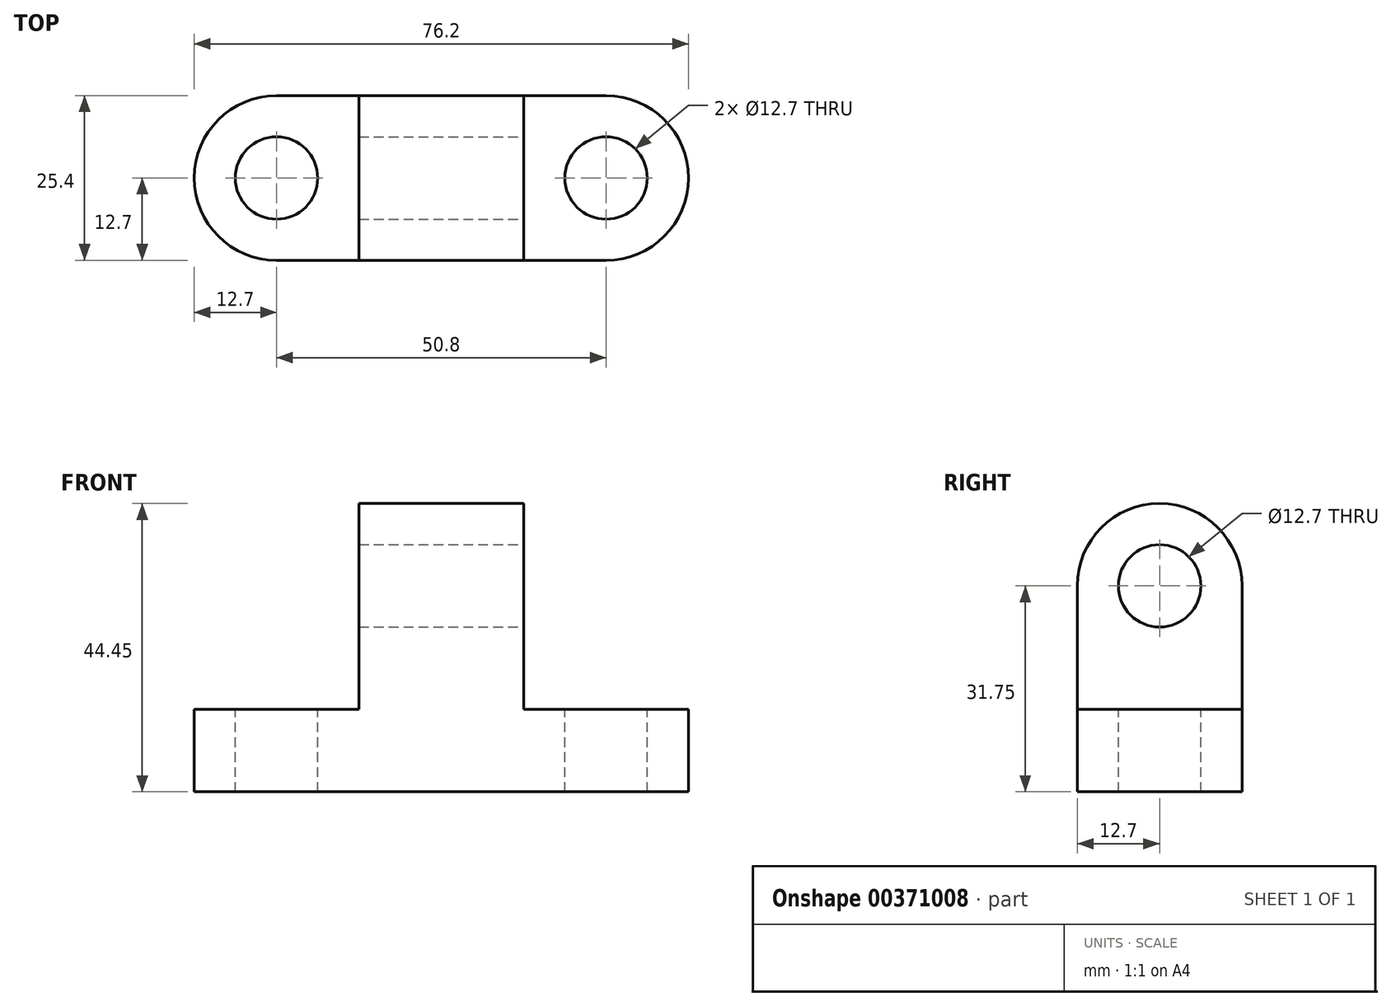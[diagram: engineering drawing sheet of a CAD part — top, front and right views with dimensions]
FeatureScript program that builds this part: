
annotation { "Feature Type Name" : "Feature", "Feature Type Description" : "" }
export const myFeature = defineFeature(function(context is Context, id is Id, definition is map)
    precondition{}
    {
        {
            var Q0;
            Q0=qCreatedBy(makeId("Front.planeOp"),FACE);
            var sketch = newSketch(context, id + "F0", { "sketchPlane" : qUnion([Q0])});
            skLineSegment(sketch, "E0", {"start": v(0, 0) * mm, "end": v(25.4, 0) * mm});
            skLineSegment(sketch, "E1", {"start": v(25.4, 0) * mm, "end": v(25.4, 44.45) * mm});
            skLineSegment(sketch, "E2", {"start": v(25.4, 44.45) * mm, "end": v(0, 44.45) * mm});
            skLineSegment(sketch, "E3", {"start": v(0, 44.45) * mm, "end": v(0, 0) * mm});
            skSolve(sketch);
        }
        {
            var Q0;
            Q0 = qSketchRegion(id + "F0", true);
            extrude(context, id + "F1", {"entities" : qUnion([Q0]), "oppositeDirection" : true, "depth" : 25.4 * mm});
        }
        {
            var Q0;
            Q0=makeQuery(id+"F1.opExtrude","CAP_EDGE",EDGE,{"disambiguationData":[OSD([sQuery(id+"F0.wireOp",EDGE,"E2")])],"isStart":true});
            var Q1;
            Q1=makeQuery(id+"F1.opExtrude","CAP_EDGE",EDGE,{"disambiguationData":[OSD([sQuery(id+"F0.wireOp",EDGE,"E2")])],"isStart":false});
            fillet(context, id + "F2", {"entities" : qUnion([Q0, Q1]), "radius" : 12.7 * mm, "tangentPropagation" : true, "allowEdgeOverflow" : false});
        }
        {
            var Q0;
            Q0=makeQuery(id+"F1.opExtrude","SWEPT_FACE",FACE,{"disambiguationData":[OSD([sQuery(id+"F0.wireOp",EDGE,"E1")])]});
            var sketch = newSketch(context, id + "F3", { "sketchPlane" : qUnion([Q0])});
            skLineSegment(sketch, "E4", {"start": v(0, 0) * mm, "end": v(0, 12.7) * mm});
            skLineSegment(sketch, "E5", {"start": v(0, 12.7) * mm, "end": v(25.4, 12.7) * mm});
            skLineSegment(sketch, "E6", {"start": v(25.4, 12.7) * mm, "end": v(25.4, 0) * mm});
            skLineSegment(sketch, "E7", {"start": v(25.4, 0) * mm, "end": v(0, 0) * mm});
            skSolve(sketch);
        }
        {
            var Q0;
            Q0=makeQuery(id+"F3.imprint","IMPRINT",FACE,{"disambiguationData":[TD([[makeQuery(id+"F3.imprint","IMPRINT",EDGE,{"derivedFrom":sQuery(id+"F3.wireOp",EDGE,"E4")}),-1.0]])]});
            extrude(context, id + "F4", {"entities" : qUnion([Q0]), "operationType" : NewBodyOperationType.ADD, "depth" : 25.4 * mm});
        }
        {
            var Q0;
            Q0=makeQuery(id+"F4.opExtrude","CAP_EDGE",EDGE,{"disambiguationData":[OSD([sQuery(id+"F3.wireOp",EDGE,"E4")])],"isStart":false});
            var Q1;
            Q1=makeQuery(id+"F4.opExtrude","CAP_EDGE",EDGE,{"disambiguationData":[OSD([sQuery(id+"F3.wireOp",EDGE,"E6")])],"isStart":false});
            fillet(context, id + "F5", {"entities" : qUnion([Q0, Q1]), "radius" : 12.7 * mm, "tangentPropagation" : true, "allowEdgeOverflow" : false});
        }
        {
            var Q0;
            Q0=makeQuery(id+"F4.opExtrude","SWEPT_FACE",FACE,{"disambiguationData":[OSD([sQuery(id+"F3.wireOp",EDGE,"E5")])]});
            var sketch = newSketch(context, id + "F6", { "sketchPlane" : qUnion([Q0])});
            skCircle(sketch, "E8", {"center": v(38.1, 12.7) * mm, "radius": 6.35 * mm});
            skSolve(sketch);
        }
        {
            var Q0;
            Q0=makeQuery(id+"F1.opExtrude","SWEPT_FACE",FACE,{"disambiguationData":[OSD([sQuery(id+"F0.wireOp",EDGE,"E3")])]});
            var sketch = newSketch(context, id + "F7", { "sketchPlane" : qUnion([Q0])});
            skLineSegment(sketch, "E9", {"start": v(0, 0) * mm, "end": v(0, 12.7) * mm});
            skLineSegment(sketch, "E10", {"start": v(0, 12.7) * mm, "end": v(-25.4, 12.7) * mm});
            skLineSegment(sketch, "E11", {"start": v(-25.4, 12.7) * mm, "end": v(-25.4, 0) * mm});
            skLineSegment(sketch, "E12", {"start": v(-25.4, 0) * mm, "end": v(0, 0) * mm});
            skSolve(sketch);
        }
        {
            var Q0;
            Q0 = qSketchRegion(id + "F7", true);
            extrude(context, id + "F8", {"entities" : qUnion([Q0]), "operationType" : NewBodyOperationType.ADD, "depth" : 25.4 * mm});
        }
        {
            var Q0;
            Q0=makeQuery(id+"F8.opExtrude","CAP_EDGE",EDGE,{"disambiguationData":[OSD([sQuery(id+"F7.wireOp",EDGE,"E11")])],"isStart":false});
            var Q1;
            Q1=makeQuery(id+"F8.opExtrude","CAP_EDGE",EDGE,{"disambiguationData":[OSD([sQuery(id+"F7.wireOp",EDGE,"E9")])],"isStart":false});
            fillet(context, id + "F9", {"entities" : qUnion([Q0, Q1]), "radius" : 12.7 * mm, "tangentPropagation" : true, "allowEdgeOverflow" : false});
        }
        {
            var Q0;
            Q0=makeQuery(id+"F8.opExtrude","SWEPT_FACE",FACE,{"disambiguationData":[OSD([sQuery(id+"F7.wireOp",EDGE,"E10")])]});
            var sketch = newSketch(context, id + "F10", { "sketchPlane" : qUnion([Q0])});
            skCircle(sketch, "E13", {"center": v(-12.7, 12.7) * mm, "radius": 6.35 * mm});
            skSolve(sketch);
        }
        {
            var Q0;
            Q0=makeQuery(id+"F1.opExtrude","SWEPT_FACE",FACE,{"disambiguationData":[OSD([sQuery(id+"F0.wireOp",EDGE,"E1")])]});
            var sketch = newSketch(context, id + "F11", { "sketchPlane" : qUnion([Q0])});
            skCircle(sketch, "E14", {"center": v(12.7, 31.75) * mm, "radius": 6.35 * mm});
            skPoint(sketch, "E15.orphan", {"position": v(12.7, 44.45) * mm});
            skSolve(sketch);
        }
        {
            var Q0;
            Q0 = qSketchRegion(id + "F11", true);
            extrude(context, id + "F12", {"entities" : qUnion([Q0]), "operationType" : NewBodyOperationType.REMOVE, "oppositeDirection" : true, "depth" : 25.4 * mm});
        }
        {
            var Q0;
            Q0 = qSketchRegion(id + "F6", true);
            extrude(context, id + "F13", {"entities" : qUnion([Q0]), "operationType" : NewBodyOperationType.REMOVE, "oppositeDirection" : true, "depth" : 25.4 * mm});
        }
        {
            var Q0;
            Q0=makeQuery(id+"F10.imprint","IMPRINT",FACE,{"disambiguationData":[TD([[makeQuery(id+"F10.imprint","IMPRINT",EDGE,{"derivedFrom":sQuery(id+"F10.wireOp",EDGE,"E13")}),1.0]])]});
            extrude(context, id + "F14", {"entities" : qUnion([Q0]), "operationType" : NewBodyOperationType.REMOVE, "oppositeDirection" : true, "depth" : 25.4 * mm});
        }
    });
